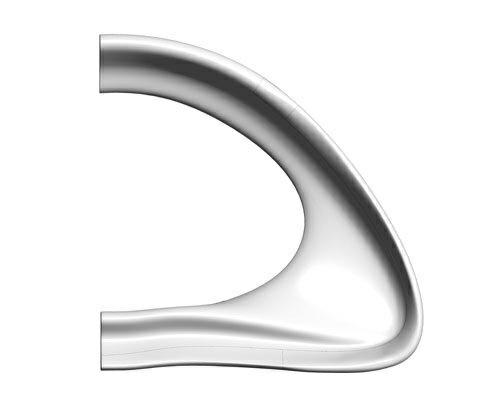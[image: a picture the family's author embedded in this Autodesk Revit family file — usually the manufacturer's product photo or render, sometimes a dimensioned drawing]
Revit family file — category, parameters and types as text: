
# Revit family: CITY ALPHABET litera „V” pionowo
name_source: partatom
category: Meble
revit_build: Autodesk Revit 2018 (Build: 20190510_1515(x64)
units: mm (PartAtom-declared; Revit-internal decimal feet)

## family parameters
Numer OmniClass = 23.40.10.11.14
Obiekt nadrzędny = Powierzchnia
Punkt obliczania pomieszczeń = Nie
Tnij formami wycięć po wczytaniu = Nie
Tytuł OmniClass = Exterior Seating
Współdzielony = Nie

## types (1)
- CITY ALPHABET litera „V”
    Domyślna rzędna = 1219 mm
    Długość = 1850 mm  [stored 6.06955 ft]
    IfcExportAs = IfcFurnishingElement
    Komentarze do typu = Ławka
    Materiał - informacja = Szeroki wybór kolorów wg palety RAL. Istnieje również możliwość specjalnego wykonania
kolorystycznego na indywidualne zapytanie klienta.
    Model = CITY ALPHABET litera „V”
    Obraz typu = V.jpg
    Producent = Astrini Design
    Szerokość = 850 mm  [stored 2.78871 ft]
    Temepratura użytkowania = -40°C do 80°C, ( -40°F do 176°F )
    URL = http://astrini-design.pl
    Waga (szacunkowo) = 80.00 kg
    Waga po wypełnieniu (szacunkowo) = 130.00 kg
    Wysokość = 1900 mm  [stored 6.2336 ft]

note: [stored X ft] marks values corroborated as IEEE doubles in the binary element streams (Revit-internal decimal feet)
